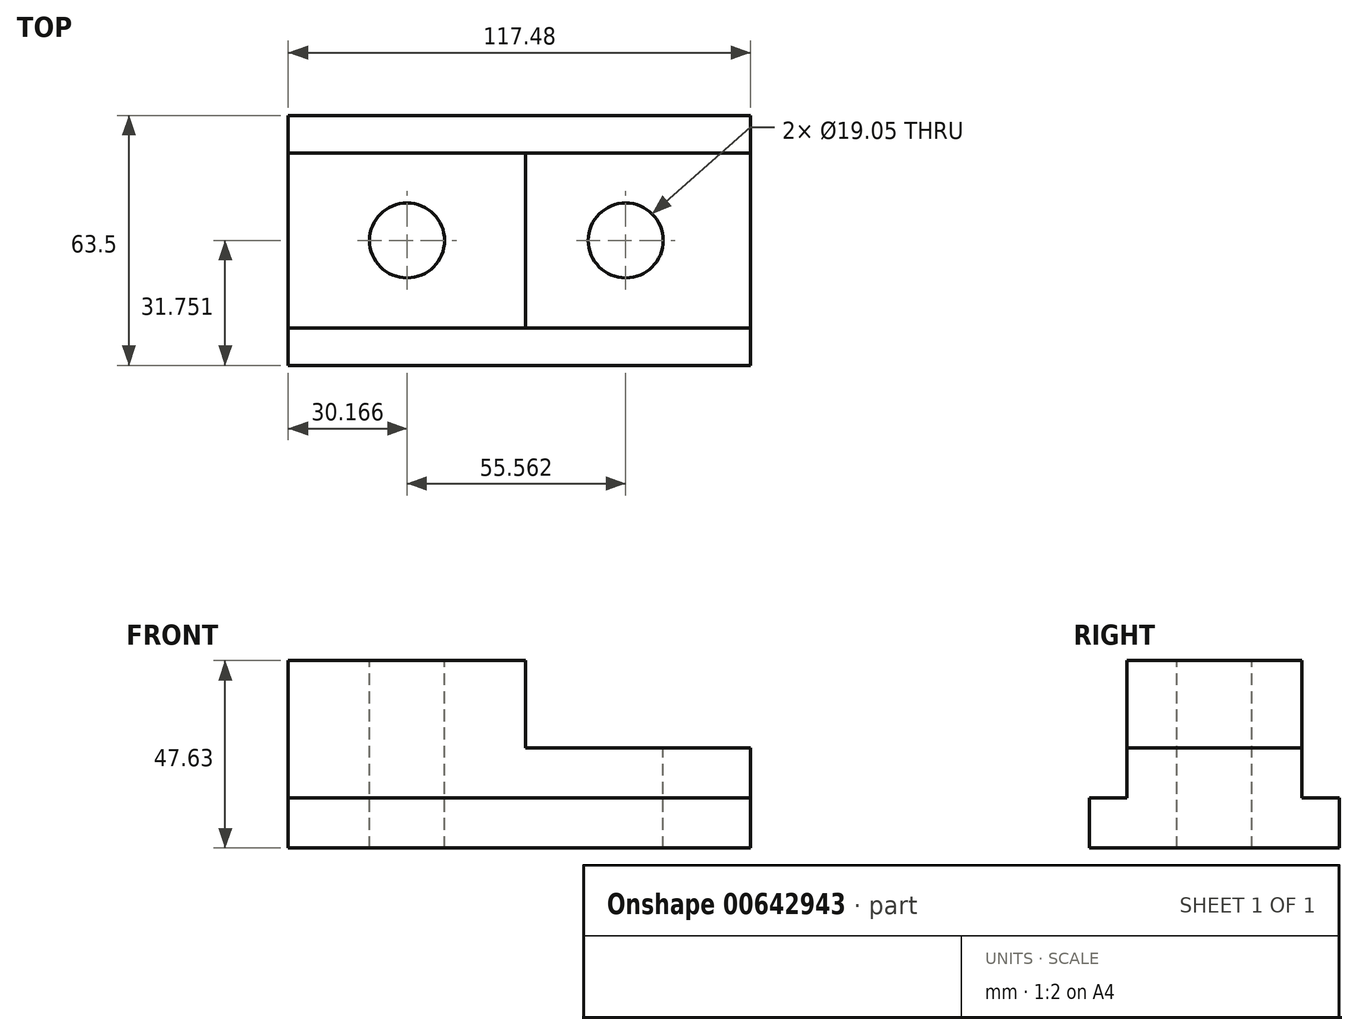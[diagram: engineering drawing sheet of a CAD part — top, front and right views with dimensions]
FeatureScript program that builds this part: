
annotation { "Feature Type Name" : "Feature", "Feature Type Description" : "" }
export const myFeature = defineFeature(function(context is Context, id is Id, definition is map)
    precondition{}
    {
        {
            var Q0;
            Q0=qCreatedBy(makeId("Top.planeOp"),FACE);
            var sketch = newSketch(context, id + "F0", { "sketchPlane" : qUnion([Q0])});
            skLineSegment(sketch, "E0.bottom", {"start": v(-64.15, 19.48) * mm, "end": v(53.33, 19.48) * mm});
            skLineSegment(sketch, "E0.top", {"start": v(-64.15, -44.02) * mm, "end": v(53.33, -44.02) * mm});
            skLineSegment(sketch, "E0.left", {"start": v(-64.15, 19.48) * mm, "end": v(-64.15, -44.02) * mm});
            skLineSegment(sketch, "E0.right", {"start": v(53.33, 19.48) * mm, "end": v(53.33, -44.02) * mm});
            skSolve(sketch);
        }
        {
            var Q0;
            Q0=makeQuery(id+"F0.imprint","IMPRINT",FACE,{"disambiguationData":[TD([[makeQuery(id+"F0.imprint","IMPRINT",EDGE,{"derivedFrom":sQuery(id+"F0.wireOp",EDGE,"E0.bottom")}),-1.0]])]});
            extrude(context, id + "F1", {"entities" : qUnion([Q0]), "depth" : 47.62 * mm, "offsetDistance" : 25.4 * mm});
        }
        {
            var Q0;
            Q0=makeQuery(id+"F1.opExtrude","SWEPT_FACE",FACE,{"disambiguationData":[OSD([sQuery(id+"F0.wireOp",EDGE,"E0.right")])]});
            var sketch = newSketch(context, id + "F2", { "sketchPlane" : qUnion([Q0])});
            skLineSegment(sketch, "E1.bottom", {"start": v(-44.02, 47.63) * mm, "end": v(-34.5, 47.63) * mm});
            skLineSegment(sketch, "E1.top", {"start": v(-44.02, 12.7) * mm, "end": v(-34.5, 12.7) * mm});
            skLineSegment(sketch, "E1.left", {"start": v(-44.02, 47.63) * mm, "end": v(-44.02, 12.7) * mm});
            skLineSegment(sketch, "E1.right", {"start": v(-34.5, 47.63) * mm, "end": v(-34.5, 12.7) * mm});
            skLineSegment(sketch, "E2.bottom", {"start": v(19.48, 47.63) * mm, "end": v(9.96, 47.63) * mm});
            skLineSegment(sketch, "E2.top", {"start": v(19.48, 12.7) * mm, "end": v(9.96, 12.7) * mm});
            skLineSegment(sketch, "E2.left", {"start": v(19.48, 47.63) * mm, "end": v(19.48, 12.7) * mm});
            skLineSegment(sketch, "E2.right", {"start": v(9.96, 47.63) * mm, "end": v(9.96, 12.7) * mm});
            skSolve(sketch);
        }
        {
            var Q0;
            Q0=makeQuery(id+"F2.imprint","IMPRINT",FACE,{"disambiguationData":[TD([[makeQuery(id+"F2.imprint","IMPRINT",EDGE,{"derivedFrom":sQuery(id+"F2.wireOp",EDGE,"E1.bottom")}),1.0]])]});
            var Q1;
            Q1=makeQuery(id+"F2.imprint","IMPRINT",FACE,{"disambiguationData":[TD([[makeQuery(id+"F2.imprint","IMPRINT",EDGE,{"derivedFrom":sQuery(id+"F2.wireOp",EDGE,"E2.bottom")}),1.0]])]});
            extrude(context, id + "F3", {"entities" : qUnion([Q0, Q1]), "operationType" : NewBodyOperationType.REMOVE, "endBound" : BoundingType.THROUGH_ALL, "oppositeDirection" : true, "depth" : 25.4 * mm, "offsetDistance" : 25.4 * mm});
        }
        {
            var Q0;
            Q0=makeQuery(id+"F1.opExtrude","CAP_FACE",FACE,{"disambiguationData":[OSD([sQuery(id+"F0.wireOp",EDGE,"E0.bottom"),sQuery(id+"F0.wireOp",EDGE,"E0.top"),sQuery(id+"F0.wireOp",EDGE,"E0.left"),sQuery(id+"F0.wireOp",EDGE,"E0.right")])],"isStart":false});
            var sketch = newSketch(context, id + "F4", { "sketchPlane" : qUnion([Q0])});
            skLineSegment(sketch, "E3.bottom", {"start": v(-3.82, 9.96) * mm, "end": v(53.33, 9.96) * mm});
            skLineSegment(sketch, "E3.top", {"start": v(-3.82, -34.5) * mm, "end": v(53.33, -34.5) * mm});
            skLineSegment(sketch, "E3.left", {"start": v(-3.82, 9.96) * mm, "end": v(-3.82, -34.5) * mm});
            skLineSegment(sketch, "E3.right", {"start": v(53.33, 9.96) * mm, "end": v(53.33, -34.5) * mm});
            skSolve(sketch);
        }
        {
            var Q0;
            Q0=makeQuery(id+"F4.imprint","IMPRINT",FACE,{"disambiguationData":[TD([[makeQuery(id+"F4.imprint","IMPRINT",EDGE,{"derivedFrom":sQuery(id+"F4.wireOp",EDGE,"E3.bottom")}),-1.0]])]});
            extrude(context, id + "F5", {"entities" : qUnion([Q0]), "operationType" : NewBodyOperationType.REMOVE, "oppositeDirection" : true, "depth" : 22.22 * mm, "offsetDistance" : 25.4 * mm});
        }
        {
            var Q0;
            Q0=makeQuery(id+"F1.opExtrude","CAP_FACE",FACE,{"disambiguationData":[OSD([sQuery(id+"F0.wireOp",EDGE,"E0.bottom"),sQuery(id+"F0.wireOp",EDGE,"E0.top"),sQuery(id+"F0.wireOp",EDGE,"E0.left"),sQuery(id+"F0.wireOp",EDGE,"E0.right")])],"isStart":false});
            var sketch = newSketch(context, id + "F6", { "sketchPlane" : qUnion([Q0])});
            skCircle(sketch, "E4", {"center": v(-33.98, -12.27) * mm, "radius": 9.53 * mm});
            skSolve(sketch);
        }
        {
            var Q0;
            Q0=makeQuery(id+"F5.boolean.opBoolean","COPY",FACE,{"derivedFrom":makeQuery(id+"F5.opExtrude","CAP_FACE",FACE,{"disambiguationData":[OSD([sQuery(id+"F4.wireOp",EDGE,"E3.bottom"),sQuery(id+"F4.wireOp",EDGE,"E3.top"),sQuery(id+"F4.wireOp",EDGE,"E3.left"),sQuery(id+"F4.wireOp",EDGE,"E3.right")])],"isStart":false})});
            var sketch = newSketch(context, id + "F7", { "sketchPlane" : qUnion([Q0])});
            skCircle(sketch, "E5", {"center": v(21.58, -12.27) * mm, "radius": 9.53 * mm});
            skPoint(sketch, "E5.centerSnap0", {"position": v(53.33, -12.27) * mm});
            skSolve(sketch);
        }
        {
            var Q0;
            Q0=makeQuery(id+"F7.imprint","IMPRINT",FACE,{"disambiguationData":[TD([[makeQuery(id+"F7.imprint","IMPRINT",EDGE,{"derivedFrom":sQuery(id+"F7.wireOp",EDGE,"E5")}),1.0]])]});
            var Q1;
            Q1=makeQuery(id+"F6.imprint","IMPRINT",FACE,{"disambiguationData":[TD([[makeQuery(id+"F6.imprint","IMPRINT",EDGE,{"derivedFrom":sQuery(id+"F6.wireOp",EDGE,"E4")}),1.0]])]});
            extrude(context, id + "F8", {"entities" : qUnion([Q0, Q1]), "operationType" : NewBodyOperationType.REMOVE, "endBound" : BoundingType.THROUGH_ALL, "oppositeDirection" : true, "depth" : 25.4 * mm, "offsetDistance" : 25.4 * mm});
        }
    });
